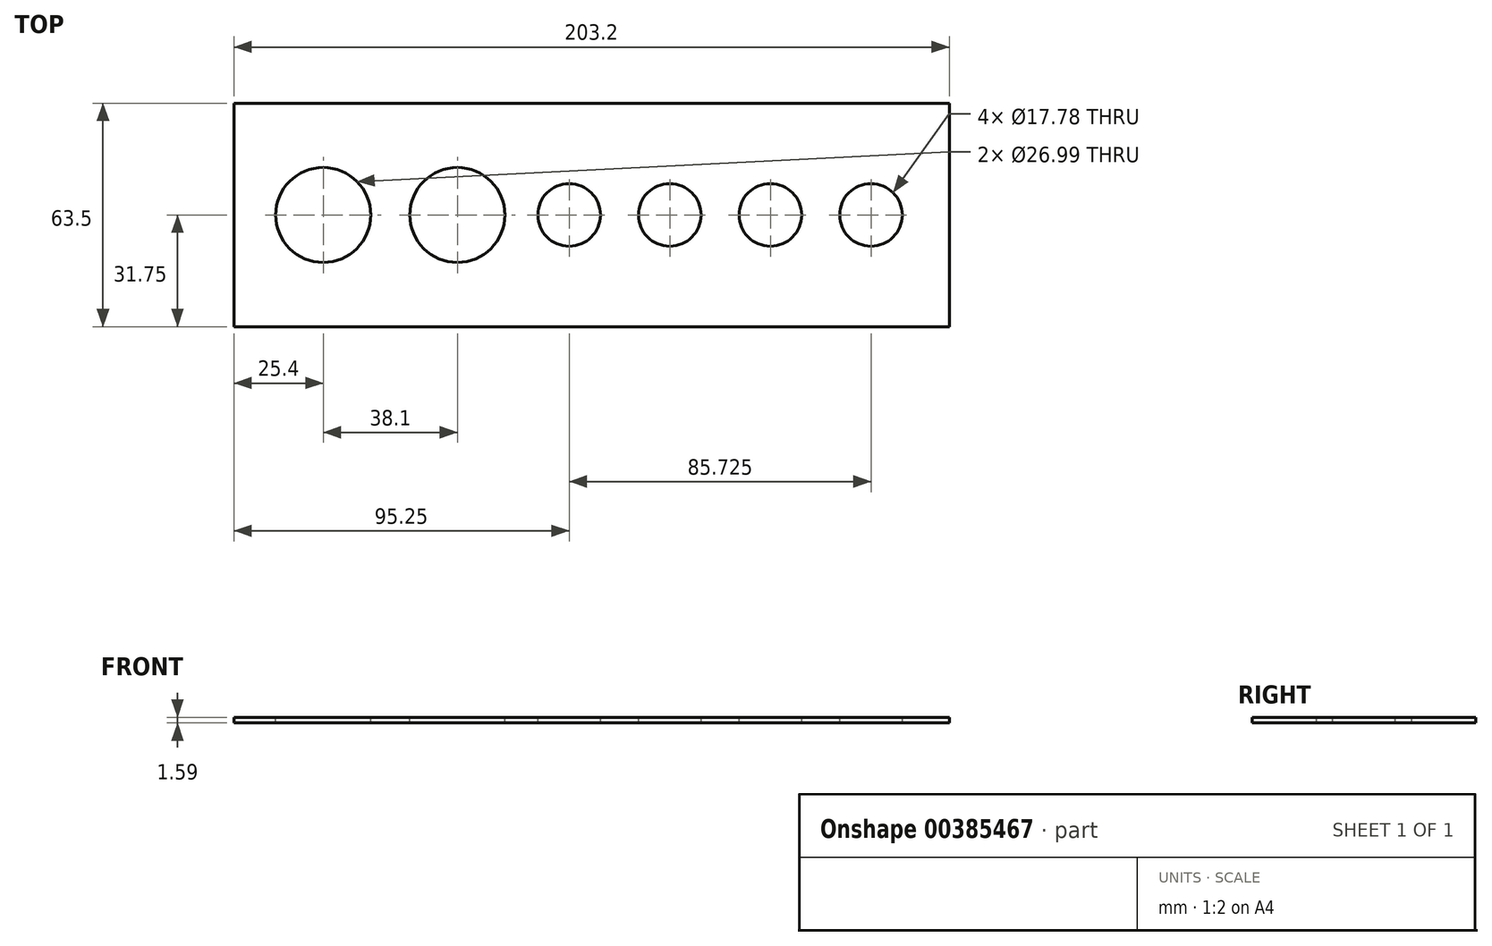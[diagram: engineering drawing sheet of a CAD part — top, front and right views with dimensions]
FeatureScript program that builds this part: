
annotation { "Feature Type Name" : "Feature", "Feature Type Description" : "" }
export const myFeature = defineFeature(function(context is Context, id is Id, definition is map)
    precondition{}
    {
        {
            var Q0;
            Q0=qCreatedBy(makeId("Top.planeOp"),FACE);
            var sketch = newSketch(context, id + "F0", { "sketchPlane" : qUnion([Q0])});
            skLineSegment(sketch, "E0.bottom", {"start": v(101.6, 31.75) * mm, "end": v(-101.6, 31.75) * mm});
            skLineSegment(sketch, "E0.top", {"start": v(101.6, -31.75) * mm, "end": v(-101.6, -31.75) * mm});
            skLineSegment(sketch, "E0.left", {"start": v(101.6, 31.75) * mm, "end": v(101.6, -31.75) * mm});
            skLineSegment(sketch, "E0.right", {"start": v(-101.6, 31.75) * mm, "end": v(-101.6, -31.75) * mm});
            skPoint(sketch, "E0.middle", {"position": v(0, 0) * mm});
            skSolve(sketch);
        }
        {
            var Q0;
            Q0 = qSketchRegion(id + "F0", true);
            extrude(context, id + "F1", {"entities" : qUnion([Q0]), "depth" : 1.59 * mm});
        }
        {
            var Q0;
            Q0=makeQuery(id+"F1.opExtrude","CAP_FACE",FACE,{"disambiguationData":[OSD([sQuery(id+"F0.wireOp",EDGE,"E0.bottom"),sQuery(id+"F0.wireOp",EDGE,"E0.top"),sQuery(id+"F0.wireOp",EDGE,"E0.left"),sQuery(id+"F0.wireOp",EDGE,"E0.right")])],"isStart":false});
            var sketch = newSketch(context, id + "F2", { "sketchPlane" : qUnion([Q0])});
            skCircle(sketch, "E1", {"center": v(-76.2, 0) * mm, "radius": 13.5 * mm});
            skCircle(sketch, "E2", {"center": v(-38.1, 0) * mm, "radius": 13.5 * mm});
            skCircle(sketch, "E3", {"center": v(-6.35, 0) * mm, "radius": 8.9 * mm});
            skCircle(sketch, "E4", {"center": v(22.23, 0) * mm, "radius": 8.9 * mm});
            skCircle(sketch, "E5", {"center": v(50.8, 0) * mm, "radius": 8.9 * mm});
            skCircle(sketch, "E6", {"center": v(79.38, 0) * mm, "radius": 8.9 * mm});
            skLineSegment(sketch, "E7", {"start": v(-101.6, 0) * mm, "end": v(101.6, 0) * mm, "construction": true});
            skSolve(sketch);
        }
        {
            var Q0;
            Q0 = qSketchRegion(id + "F2", true);
            extrude(context, id + "F3", {"entities" : qUnion([Q0]), "operationType" : NewBodyOperationType.REMOVE, "oppositeDirection" : true, "depth" : 25.4 * mm});
        }
    });
